# Revit family: Drinking_Fountain-Haws_Corporation-Wall_Mounted_1431 new
name_source: partatom
category: Plumbing Fixtures
revit_build: Autodesk Revit Architecture 2015 (Build: 20160512_1515(x64)
units: mm (PartAtom-declared; Revit-internal decimal feet)

## types (1)
- 1431
    Assembly Code = D2010810
    Basin Height = 0' - 6"
    Bowl = Metal - Haws Corporation - White Enameled Iron
    CW Connection = Yes
    CWFU = 1
    Cost = 0 $
    Cost Note = For Cost information please visit the Resource tab in the Product Page URL
    Default Elevation = 2' - 3"
    Description = Dual bubbler heads locked to main bowl prevent against vandals
    Flow = 0 GPM
    Fountain Level = 2' - 3"
    HW Connection = No
    HWFU = 0
    Keynote = 15410.A1
    Manufacturer = Haws Corporation
    Model = 1431
    Product Documentation Link = https://www.hawsco.com
    Product Page URL = http://www.hawsco.com
    Sanitary Radius = 0' - 0 3/4"
    Series = The multi bubbler Haws 1431 enameled iron, barrie-rfree drinking fountain
    Supply Radius = 0' - 0 3/16"
    Trap = Metal - Haws Corporation - White Enameled Iron
    Tubing = Metal - Haws Corporation - Copper
    Type Comments = Gleaming white enameled iron construction
    URL = http://www.hawsco.com
    Vent Connection = No
    Version = 2014-v2.0a
    WFU = 1
    Waste Connection = Yes
    Waste Level = 2' - 1 7/8"

## geometry (parser evidence)
native form markers: Blend x8, Sweep x4
no freeform markers — native parametric forms only
